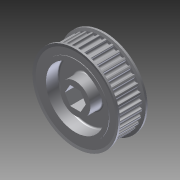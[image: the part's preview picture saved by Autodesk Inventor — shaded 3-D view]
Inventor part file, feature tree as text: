
AUTODESK INVENTOR PART (.ipt)
format: ipt  version: 2014 SP1 (Build 180222100, 222)  size: 1,033,728 bytes
history: native  units: in
note: dims shown in document units (in); Inventor stores cm internally (conversion verified against a paired STEP export)
features: mirror x1, other x1, imported_body x1
ambient origin geometry x8: Origin, YZ Plane, XZ Plane, XY Plane, X Axis, Y Axis, Z Axis, Center Point
bodies: Body1 (feature_tree)
feature tree (3):
  mirror  "Mirror1"
  other  "217-3232-STEP1"
  imported_body  "Base1"
